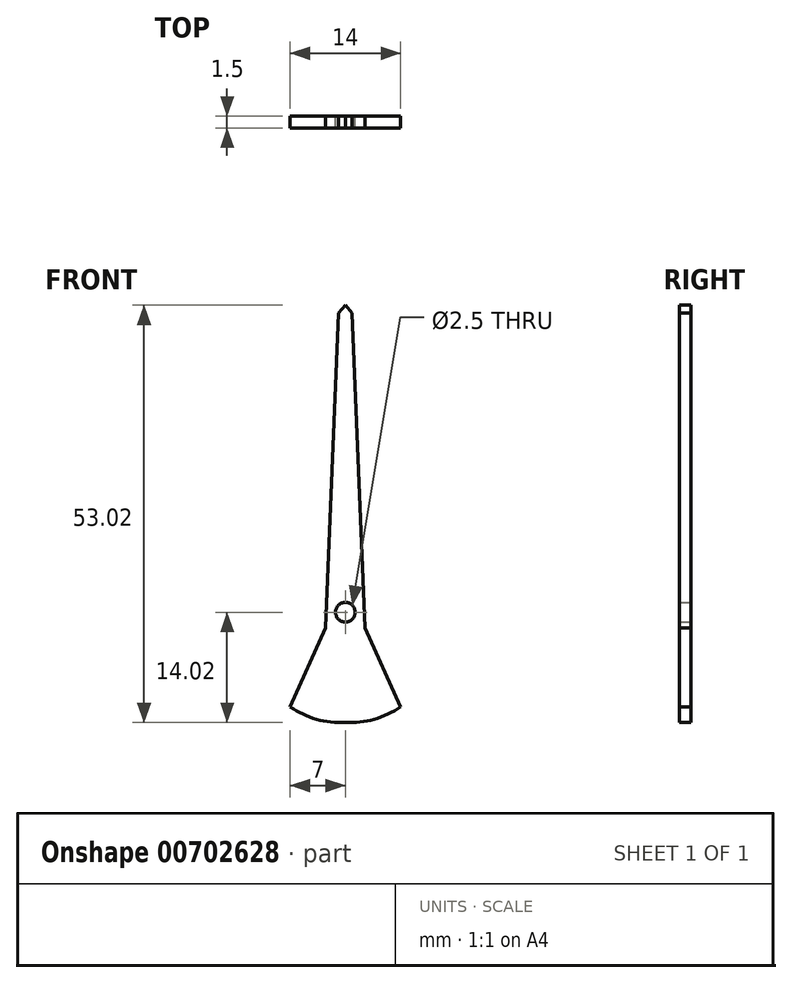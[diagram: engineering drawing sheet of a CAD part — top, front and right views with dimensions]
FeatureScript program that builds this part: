
annotation { "Feature Type Name" : "Feature", "Feature Type Description" : "" }
export const myFeature = defineFeature(function(context is Context, id is Id, definition is map)
    precondition{}
    {
        {
            var Q0;
            Q0=qCreatedBy(makeId("Front.planeOp"),FACE);
            var sketch = newSketch(context, id + "F0", { "sketchPlane" : qUnion([Q0])});
            skCircle(sketch, "E0", {"center": v(0, 0) * mm, "radius": 1.25 * mm});
            skLineSegment(sketch, "E1", {"start": v(0, 12.85) * mm, "end": v(0, -13.32) * mm, "construction": true});
            skLineSegment(sketch, "E2", {"start": v(0, 39) * mm, "end": v(-0.85, 38) * mm});
            skLineSegment(sketch, "E3", {"start": v(-0.85, 38) * mm, "end": v(-2.5, -2) * mm});
            skLineSegment(sketch, "E4", {"start": v(-2.5, -2) * mm, "end": v(-7, -12) * mm});
            skArc(sketch, "E5", {"start": v(-7, -12) * mm, "mid": v(-3.67, -13.6) * mm, "end": v(0, -14) * mm});
            skArc(sketch, "E6.MirrorCS", {"start": v(7, -12) * mm, "mid": v(3.67, -13.6) * mm, "end": v(0, -14) * mm});
            skLineSegment(sketch, "E7.MirrorCS", {"start": v(2.5, -2) * mm, "end": v(7, -12) * mm});
            skLineSegment(sketch, "E8.MirrorCS", {"start": v(0, 39) * mm, "end": v(0.85, 38) * mm});
            skLineSegment(sketch, "E9.MirrorCS", {"start": v(0.85, 38) * mm, "end": v(2.5, -2) * mm});
            skSolve(sketch);
        }
        {
            var Q0;
            Q0 = qSketchRegion(id + "F0", true);
            extrude(context, id + "F1", {"entities" : qUnion([Q0]), "depth" : 1.5 * mm, "offsetDistance" : 25 * mm});
        }
    });
